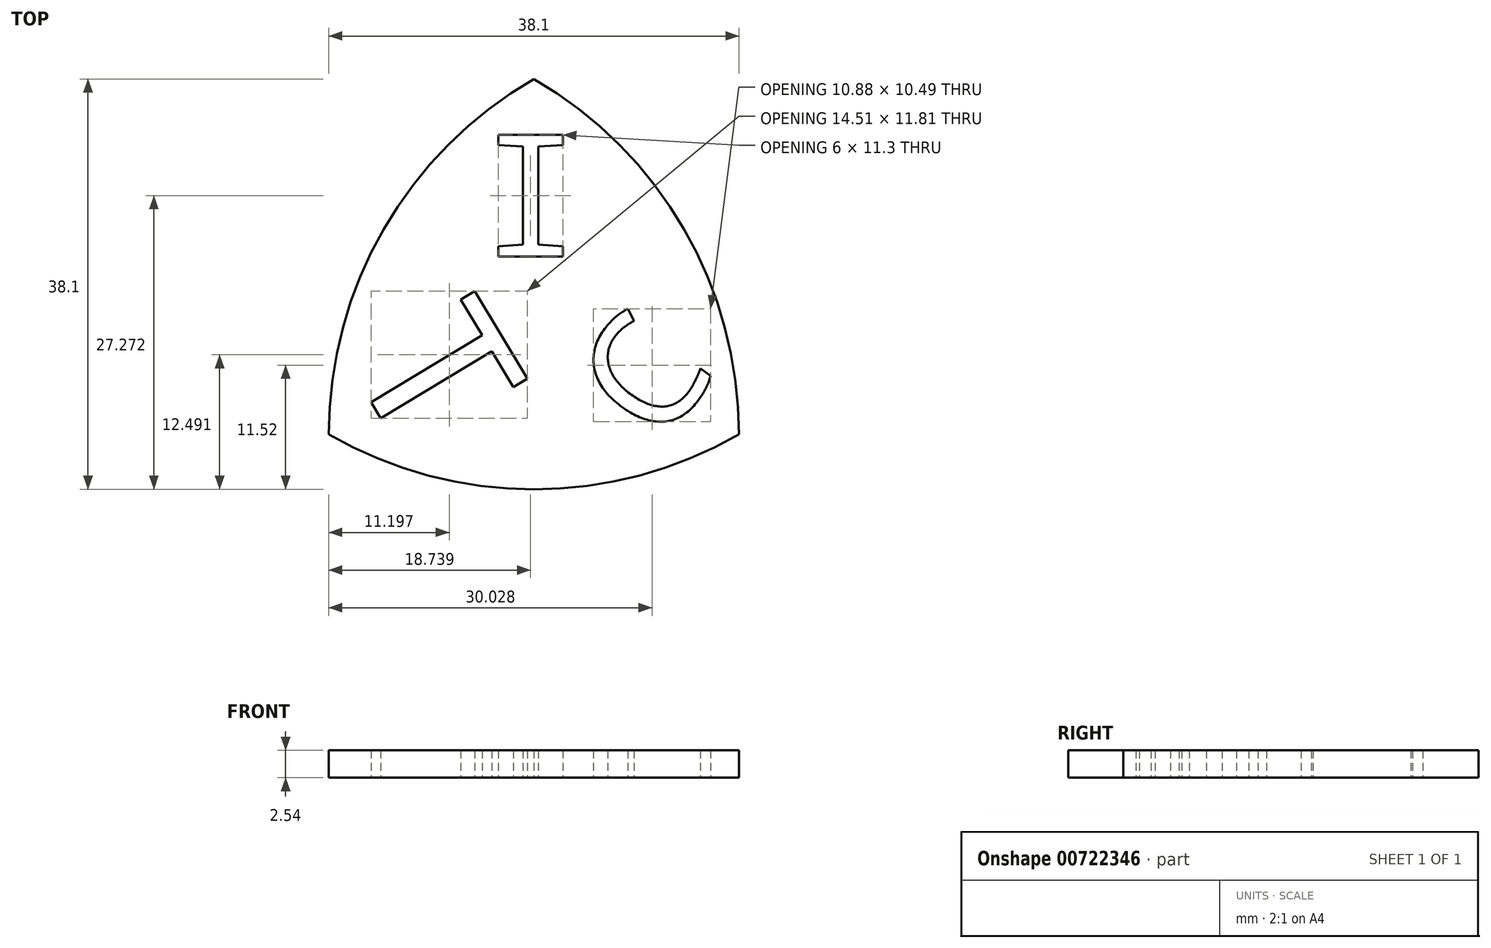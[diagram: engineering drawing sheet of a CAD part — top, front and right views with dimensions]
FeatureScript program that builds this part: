
annotation { "Feature Type Name" : "Feature", "Feature Type Description" : "" }
export const myFeature = defineFeature(function(context is Context, id is Id, definition is map)
    precondition{}
    {
        {
            var Q0;
            Q0=qCreatedBy(makeId("Top.planeOp"),FACE);
            var sketch = newSketch(context, id + "F0", { "sketchPlane" : qUnion([Q0])});
            skCircle(sketch, "E0", {"center": v(0, 0) * mm, "radius": 38.1 * mm});
            skSolve(sketch);
        }
        {
            var Q0;
            Q0=qCreatedBy(makeId("Top.planeOp"),FACE);
            var sketch = newSketch(context, id + "F1", { "sketchPlane" : qUnion([Q0])});
            skCircle(sketch, "E1", {"center": v(-38.1, 0) * mm, "radius": 38.1 * mm});
            skSolve(sketch);
        }
        {
            var Q0;
            Q0=qCreatedBy(makeId("Top.planeOp"),FACE);
            var sketch = newSketch(context, id + "F2", { "sketchPlane" : qUnion([Q0])});
            skCircle(sketch, "E2", {"center": v(-19.05, 33) * mm, "radius": 38.1 * mm});
            skSolve(sketch);
        }
        {
            var Q0;
            Q0=makeQuery(id+"F0.imprint","IMPRINT",FACE,{"disambiguationData":[TD([[makeQuery(id+"F0.imprint","IMPRINT",EDGE,{"derivedFrom":sQuery(id+"F0.wireOp",EDGE,"E0")}),1.0]])]});
            extrude(context, id + "F3", {"entities" : qUnion([Q0]), "depth" : 2.54 * mm, "offsetDistance" : 25.4 * mm});
        }
        {
            var Q0;
            Q0 = qSketchRegion(id + "F1", true);
            extrude(context, id + "F4", {"entities" : qUnion([Q0]), "depth" : 2.54 * mm, "offsetDistance" : 25.4 * mm});
        }
        {
            var Q0;
            Q0=makeQuery(id+"F2.imprint","IMPRINT",FACE,{"disambiguationData":[TD([[makeQuery(id+"F2.imprint","IMPRINT",EDGE,{"derivedFrom":sQuery(id+"F2.wireOp",EDGE,"E2")}),1.0]])]});
            extrude(context, id + "F5", {"entities" : qUnion([Q0]), "depth" : 2.54 * mm, "offsetDistance" : 25.4 * mm});
        }
        {
            var Q0;
            Q0=makeQuery(id+"F3.opExtrude","SWEPT_BODY",BODY,{"disambiguationData":[OSD([sQuery(id+"F0.wireOp",EDGE,"E0")])]});
            var Q1;
            Q1=makeQuery(id+"F5.opExtrude","SWEPT_BODY",BODY,{"disambiguationData":[OSD([sQuery(id+"F2.wireOp",EDGE,"E2")])]});
            var Q2;
            Q2=makeQuery(id+"F4.opExtrude","SWEPT_BODY",BODY,{"disambiguationData":[OSD([sQuery(id+"F1.wireOp",EDGE,"E1")])]});
            booleanBodies(context, id + "F6", {"operationType" : BooleanOperationType.INTERSECTION, "tools" : qUnion([Q0, Q1, Q2])});
        }
        {
            var Q0;
            Q0=qCreatedBy(makeId("Top.planeOp"),FACE);
            var sketch = newSketch(context, id + "F7", { "sketchPlane" : qUnion([Q0])});
            skText(sketch, "E3", { "text": "C", "fontName": "DroidSansMono.ttf"});
            skText(sketch, "E4", { "text": "I", "fontName": "DroidSansMono.ttf"});
            skText(sketch, "E5", { "text": "T", "fontName": "DroidSansMono.ttf"});
            const initialGuessF7  = {"E3": [-0.0073, -0.0013, 0.59862, 0.80103, 0.01073], "E4": [-0.0241, 0.01652, 1, 0, 0.0114], "E5": [-0.03665, 0.0071, 0.51667, -0.85619, 0.01368]};
            skSetInitialGuess(sketch, initialGuessF7);
            skSolve(sketch);
        }
        {
            var Q0;
            Q0 = qSketchRegion(id + "F7", true);
            extrude(context, id + "F8", {"entities" : qUnion([Q0]), "depth" : 2.54 * mm, "offsetDistance" : 25.4 * mm});
        }
        {
            var Q0;
            Q0=makeQuery(id+"F8.opExtrude","SWEPT_BODY",BODY,{"disambiguationData":[OSD([sQuery(id+"F7.wireOp",EDGE,"E3.sketch_text.stroke-0"),sQuery(id+"F7.wireOp",EDGE,"E3.sketch_text.stroke-1"),sQuery(id+"F7.wireOp",EDGE,"E3.sketch_text.stroke-2"),sQuery(id+"F7.wireOp",EDGE,"E3.sketch_text.stroke-3"),sQuery(id+"F7.wireOp",EDGE,"E3.sketch_text.stroke-4"),sQuery(id+"F7.wireOp",EDGE,"E3.sketch_text.stroke-5"),sQuery(id+"F7.wireOp",EDGE,"E3.sketch_text.stroke-6"),sQuery(id+"F7.wireOp",EDGE,"E3.sketch_text.stroke-7"),sQuery(id+"F7.wireOp",EDGE,"E3.sketch_text.stroke-8"),sQuery(id+"F7.wireOp",EDGE,"E3.sketch_text.stroke-9"),sQuery(id+"F7.wireOp",EDGE,"E3.sketch_text.stroke-10"),sQuery(id+"F7.wireOp",EDGE,"E3.sketch_text.stroke-11"),sQuery(id+"F7.wireOp",EDGE,"E3.sketch_text.stroke-12"),sQuery(id+"F7.wireOp",EDGE,"E3.sketch_text.stroke-13")])]});
            var Q1;
            Q1=makeQuery(id+"F8.opExtrude","SWEPT_BODY",BODY,{"disambiguationData":[OSD([sQuery(id+"F7.wireOp",EDGE,"E5.sketch_text.stroke-0"),sQuery(id+"F7.wireOp",EDGE,"E5.sketch_text.stroke-1"),sQuery(id+"F7.wireOp",EDGE,"E5.sketch_text.stroke-2"),sQuery(id+"F7.wireOp",EDGE,"E5.sketch_text.stroke-3"),sQuery(id+"F7.wireOp",EDGE,"E5.sketch_text.stroke-4"),sQuery(id+"F7.wireOp",EDGE,"E5.sketch_text.stroke-5"),sQuery(id+"F7.wireOp",EDGE,"E5.sketch_text.stroke-6"),sQuery(id+"F7.wireOp",EDGE,"E5.sketch_text.stroke-7")])]});
            var Q2;
            Q2=makeQuery(id+"F8.opExtrude","SWEPT_BODY",BODY,{"disambiguationData":[OSD([sQuery(id+"F7.wireOp",EDGE,"E4.sketch_text.stroke-0"),sQuery(id+"F7.wireOp",EDGE,"E4.sketch_text.stroke-1"),sQuery(id+"F7.wireOp",EDGE,"E4.sketch_text.stroke-2"),sQuery(id+"F7.wireOp",EDGE,"E4.sketch_text.stroke-3"),sQuery(id+"F7.wireOp",EDGE,"E4.sketch_text.stroke-4"),sQuery(id+"F7.wireOp",EDGE,"E4.sketch_text.stroke-5"),sQuery(id+"F7.wireOp",EDGE,"E4.sketch_text.stroke-6"),sQuery(id+"F7.wireOp",EDGE,"E4.sketch_text.stroke-7"),sQuery(id+"F7.wireOp",EDGE,"E4.sketch_text.stroke-8"),sQuery(id+"F7.wireOp",EDGE,"E4.sketch_text.stroke-9"),sQuery(id+"F7.wireOp",EDGE,"E4.sketch_text.stroke-10"),sQuery(id+"F7.wireOp",EDGE,"E4.sketch_text.stroke-11")])]});
            var Q3;
            Q3=makeQuery(id+"F6.opBoolean","INTERSECT",BODY,{"derivedFrom":[makeQuery(id+"F3.opExtrude","SWEPT_BODY",BODY,{"disambiguationData":[OSD([sQuery(id+"F0.wireOp",EDGE,"E0")])]}),makeQuery(id+"F4.opExtrude","SWEPT_BODY",BODY,{"disambiguationData":[OSD([sQuery(id+"F1.wireOp",EDGE,"E1")])]}),makeQuery(id+"F5.opExtrude","SWEPT_BODY",BODY,{"disambiguationData":[OSD([sQuery(id+"F2.wireOp",EDGE,"E2")])]})]});
            booleanBodies(context, id + "F9", {"operationType" : BooleanOperationType.SUBTRACTION, "tools" : qUnion([Q0, Q1, Q2]), "targets" : qUnion([Q3])});
        }
    });
